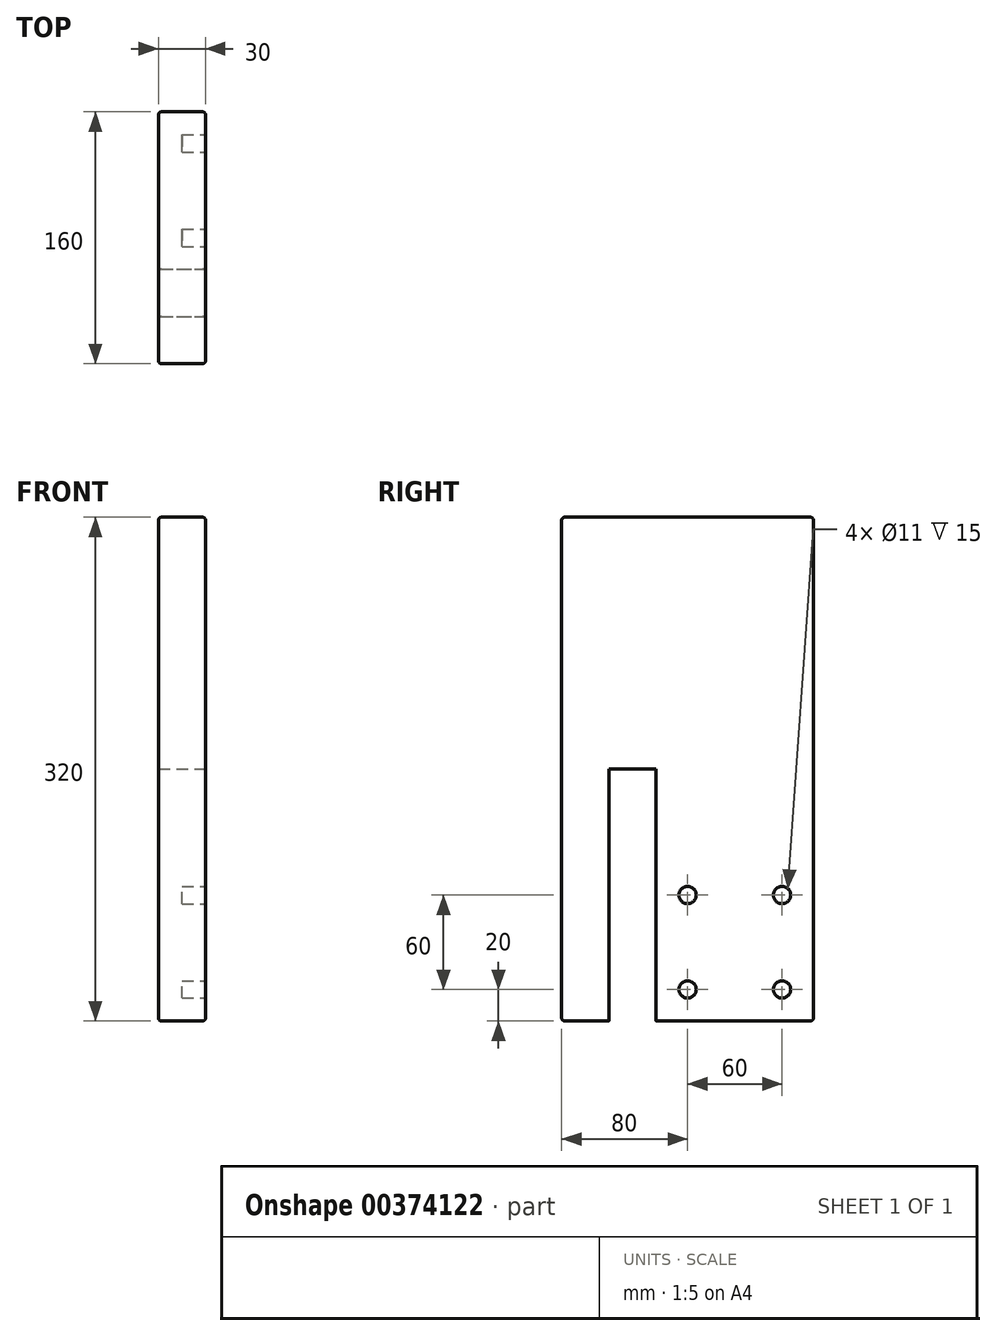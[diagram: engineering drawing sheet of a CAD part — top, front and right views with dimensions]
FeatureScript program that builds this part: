
annotation { "Feature Type Name" : "Feature", "Feature Type Description" : "" }
export const myFeature = defineFeature(function(context is Context, id is Id, definition is map)
    precondition{}
    {
        {
            var Q0;
            Q0=qCreatedBy(makeId("Top.planeOp"),FACE);
            var sketch = newSketch(context, id + "F0", { "sketchPlane" : qUnion([Q0])});
            skLineSegment(sketch, "E0.bottom", {"start": v(227.83, 174.75) * mm, "end": v(-227.83, 174.75) * mm});
            skLineSegment(sketch, "E0.top", {"start": v(227.83, -174.75) * mm, "end": v(-227.83, -174.75) * mm});
            skLineSegment(sketch, "E0.left", {"start": v(227.83, 174.75) * mm, "end": v(227.83, -174.75) * mm});
            skLineSegment(sketch, "E0.right", {"start": v(-227.83, 174.75) * mm, "end": v(-227.83, -174.75) * mm});
            skPoint(sketch, "E0.middle", {"position": v(0, 0) * mm});
            skSolve(sketch);
        }
        {
            var Q0;
            Q0=makeQuery(id+"F0.imprint","IMPRINT",FACE,{"disambiguationData":[TD([[makeQuery(id+"F0.imprint","IMPRINT",EDGE,{"derivedFrom":sQuery(id+"F0.wireOp",EDGE,"E0.bottom")}),1.0]])]});
            var sketch = newSketch(context, id + "F1", { "sketchPlane" : qUnion([Q0])});
            skLineSegment(sketch, "E1.bottom", {"start": v(15, 80) * mm, "end": v(-15, 80) * mm});
            skLineSegment(sketch, "E1.top", {"start": v(15, -80) * mm, "end": v(-15, -80) * mm});
            skLineSegment(sketch, "E1.left", {"start": v(15, 80) * mm, "end": v(15, -80) * mm});
            skLineSegment(sketch, "E1.right", {"start": v(-15, 80) * mm, "end": v(-15, -80) * mm});
            skPoint(sketch, "E1.middle", {"position": v(0, 0) * mm});
            skSolve(sketch);
        }
        {
            var Q0;
            Q0 = qSketchRegion(id + "F1", true);
            extrude(context, id + "F2", {"entities" : qUnion([Q0]), "depth" : 320 * mm, "symmetric" : true});
        }
        {
            var Q0;
            Q0=makeQuery(id+"F2.opExtrude","SWEPT_FACE",FACE,{"disambiguationData":[OSD([sQuery(id+"F1.wireOp",EDGE,"E1.left")])]});
            var Q1;
            Q1=makeQuery(id+"F2.opExtrude","SWEPT_FACE",FACE,{"disambiguationData":[OSD([sQuery(id+"F1.wireOp",EDGE,"E1.right")])]});
            var Q2;
            Q2=makeQuery(id+"F2.opExtrude","CAP_FACE",FACE,{"disambiguationData":[OSD([sQuery(id+"F1.wireOp",EDGE,"E1.bottom"),sQuery(id+"F1.wireOp",EDGE,"E1.top"),sQuery(id+"F1.wireOp",EDGE,"E1.left"),sQuery(id+"F1.wireOp",EDGE,"E1.right")])],"isStart":true});
            var Q3;
            Q3=makeQuery(id+"F2.opExtrude","SWEPT_FACE",FACE,{"disambiguationData":[OSD([sQuery(id+"F1.wireOp",EDGE,"E1.bottom")])]});
            var Q4;
            Q4=makeQuery(id+"F2.opExtrude","CAP_FACE",FACE,{"disambiguationData":[OSD([sQuery(id+"F1.wireOp",EDGE,"E1.bottom"),sQuery(id+"F1.wireOp",EDGE,"E1.top"),sQuery(id+"F1.wireOp",EDGE,"E1.left"),sQuery(id+"F1.wireOp",EDGE,"E1.right")])],"isStart":false});
            var Q5;
            Q5=makeQuery(id+"F2.opExtrude","SWEPT_FACE",FACE,{"disambiguationData":[OSD([sQuery(id+"F1.wireOp",EDGE,"E1.top")])]});
            fillet(context, id + "F3", {"entities" : qUnion([Q0, Q1, Q2, Q3, Q4, Q5]), "radius" : 2 * mm, "tangentPropagation" : true, "allowEdgeOverflow" : false});
        }
        {
            var Q0;
            Q0=makeQuery(id+"F2.opExtrude","SWEPT_FACE",FACE,{"disambiguationData":[OSD([sQuery(id+"F1.wireOp",EDGE,"E1.left")])]});
            var sketch = newSketch(context, id + "F4", { "sketchPlane" : qUnion([Q0])});
            skLineSegment(sketch, "E2.bottom", {"start": v(-50, -160) * mm, "end": v(-20, -160) * mm});
            skLineSegment(sketch, "E2.top", {"start": v(-50, 0) * mm, "end": v(-20, 0) * mm});
            skLineSegment(sketch, "E2.left", {"start": v(-50, -160) * mm, "end": v(-50, 0) * mm});
            skLineSegment(sketch, "E2.right", {"start": v(-20, -160) * mm, "end": v(-20, 0) * mm});
            skCircle(sketch, "E3", {"center": v(60, -140) * mm, "radius": 5.5 * mm});
            skCircle(sketch, "E4.0.1.0", {"center": v(60, -80) * mm, "radius": 5.5 * mm});
            skCircle(sketch, "E4.1.0.0", {"center": v(0, -140) * mm, "radius": 5.5 * mm});
            skCircle(sketch, "E4.1.1.0", {"center": v(0, -80) * mm, "radius": 5.5 * mm});
            skLineSegment(sketch, "E4.direction1", {"start": v(60, -140) * mm, "end": v(0, -140) * mm, "construction": true});
            skLineSegment(sketch, "E4.direction2", {"start": v(60, -140) * mm, "end": v(60, -80) * mm, "construction": true});
            skSolve(sketch);
        }
        {
            var Q0;
            {var subQ0=sQuery(id+"F4.wireOp",EDGE,"E2.top");Q0=makeQuery(id+"F4.imprint","IMPRINT",FACE,{"disambiguationData":[TD([[makeQuery(id+"F4.imprint","IMPRINT",EDGE,{"derivedFrom":subQ0}),-1.0]])]});}
            var Q1;
            {var subQ0=sQuery(id+"F4.wireOp",EDGE,"E2.bottom");Q1=makeQuery(id+"F4.imprint","IMPRINT",FACE,{"disambiguationData":[TD([[makeQuery(id+"F4.imprint","IMPRINT",EDGE,{"derivedFrom":subQ0}),1.0]])]});}
            extrude(context, id + "F5", {"entities" : qUnion([Q0, Q1]), "operationType" : NewBodyOperationType.REMOVE, "endBound" : BoundingType.THROUGH_ALL, "oppositeDirection" : true, "depth" : 25 * mm});
        }
        {
            var Q0;
            Q0=makeQuery(id+"F4.imprint","IMPRINT",FACE,{"disambiguationData":[TD([[makeQuery(id+"F4.imprint","IMPRINT",EDGE,{"derivedFrom":sQuery(id+"F4.wireOp",EDGE,"E3")}),1.0]])]});
            var Q1;
            Q1=makeQuery(id+"F4.imprint","IMPRINT",FACE,{"disambiguationData":[TD([[makeQuery(id+"F4.imprint","IMPRINT",EDGE,{"derivedFrom":sQuery(id+"F4.wireOp",EDGE,"E4.1.0.0")}),1.0]])]});
            var Q2;
            Q2=makeQuery(id+"F4.imprint","IMPRINT",FACE,{"disambiguationData":[TD([[makeQuery(id+"F4.imprint","IMPRINT",EDGE,{"derivedFrom":sQuery(id+"F4.wireOp",EDGE,"E4.1.1.0")}),1.0]])]});
            var Q3;
            Q3=makeQuery(id+"F4.imprint","IMPRINT",FACE,{"disambiguationData":[TD([[makeQuery(id+"F4.imprint","IMPRINT",EDGE,{"derivedFrom":sQuery(id+"F4.wireOp",EDGE,"E4.0.1.0")}),1.0]])]});
            extrude(context, id + "F6", {"entities" : qUnion([Q0, Q1, Q2, Q3]), "operationType" : NewBodyOperationType.REMOVE, "oppositeDirection" : true, "depth" : 15 * mm});
        }
    });
